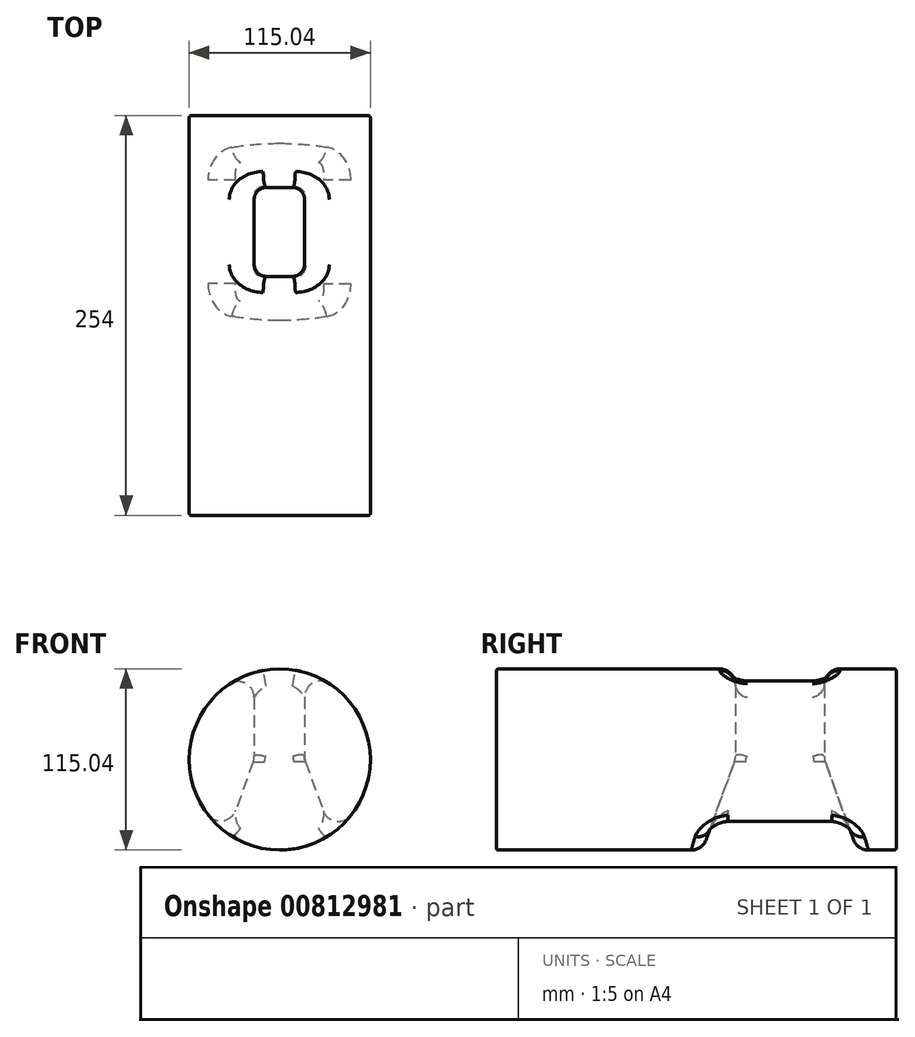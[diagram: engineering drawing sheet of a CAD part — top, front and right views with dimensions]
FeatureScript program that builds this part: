
annotation { "Feature Type Name" : "Feature", "Feature Type Description" : "" }
export const myFeature = defineFeature(function(context is Context, id is Id, definition is map)
    precondition{}
    {
        {
            var Q0;
            Q0=qCreatedBy(makeId("Front.planeOp"),FACE);
            var sketch = newSketch(context, id + "F0", { "sketchPlane" : qUnion([Q0])});
            skCircle(sketch, "E0", {"center": v(0, 0) * mm, "radius": 57.52 * mm});
            skSolve(sketch);
        }
        {
            var Q0;
            Q0 = qSketchRegion(id + "F0", true);
            extrude(context, id + "F1", {"entities" : qUnion([Q0]), "depth" : 254 * mm, "offsetDistance" : 25.4 * mm});
        }
        {
            var Q0;
            Q0=qCreatedBy(makeId("Top.planeOp"),FACE);
            var sketch = newSketch(context, id + "F2", { "sketchPlane" : qUnion([Q0])});
            skLineSegment(sketch, "E1.top", {"start": v(0, -45.7) * mm, "end": v(15.74, -45.7) * mm});
            skLineSegment(sketch, "E2.bottom", {"start": v(15.74, -45.7) * mm, "end": v(-16.26, -45.7) * mm});
            skLineSegment(sketch, "E2.top", {"start": v(15.74, -102.18) * mm, "end": v(-16.26, -102.18) * mm});
            skLineSegment(sketch, "E2.left", {"start": v(15.74, -45.7) * mm, "end": v(15.74, -102.18) * mm});
            skLineSegment(sketch, "E2.right", {"start": v(-16.26, -45.7) * mm, "end": v(-16.26, -102.18) * mm});
            skSolve(sketch);
        }
        {
            var Q0;
            Q0 = qSketchRegion(id + "F2", true);
            extrude(context, id + "F3", {"entities" : qUnion([Q0]), "operationType" : NewBodyOperationType.REMOVE, "oppositeDirection" : true, "depth" : 117.35 * mm, "offsetDistance" : 25.4 * mm, "hasDraft" : true, "draftAngle" : 20 * degree});
        }
        {
            var Q0;
            Q0=makeQuery(id+"F3.boolean.opBoolean","COPY",FACE,{"derivedFrom":makeQuery(id+"F3.opExtrude","CAP_FACE",FACE,{"disambiguationData":[OSD([sQuery(id+"F2.wireOp",EDGE,"E2.bottom"),sQuery(id+"F2.wireOp",EDGE,"E2.top"),sQuery(id+"F2.wireOp",EDGE,"E2.left"),sQuery(id+"F2.wireOp",EDGE,"E2.right")])],"isStart":true})});
            extrude(context, id + "F4", {"entities" : qUnion([Q0]), "operationType" : NewBodyOperationType.REMOVE, "oppositeDirection" : true, "depth" : 107.44 * mm, "offsetDistance" : 25.4 * mm});
        }
        {
            var Q0;
            Q0=makeQuery(id+"F3.boolean.opBoolean","COPY",EDGE,{"derivedFrom":makeQuery(id+"F3.opExtrude","SWEPT_EDGE",EDGE,{"disambiguationData":[OSD([sQuery(id+"F2.wireOp",EDGE,"E2.bottom"),sQuery(id+"F2.wireOp",EDGE,"E2.left")])]})});
            var Q1;
            Q1=makeQuery(id+"F3.boolean.opBoolean","COPY",EDGE,{"derivedFrom":makeQuery(id+"F3.opExtrude","SWEPT_EDGE",EDGE,{"disambiguationData":[OSD([sQuery(id+"F2.wireOp",EDGE,"E2.top"),sQuery(id+"F2.wireOp",EDGE,"E2.left")])]})});
            var Q2;
            Q2=makeQuery(id+"F3.boolean.opBoolean","COPY",EDGE,{"derivedFrom":makeQuery(id+"F3.opExtrude","SWEPT_EDGE",EDGE,{"disambiguationData":[OSD([sQuery(id+"F2.wireOp",EDGE,"E2.top"),sQuery(id+"F2.wireOp",EDGE,"E2.right")])]})});
            var Q3;
            Q3=makeQuery(id+"F3.boolean.opBoolean","COPY",EDGE,{"derivedFrom":makeQuery(id+"F3.opExtrude","SWEPT_EDGE",EDGE,{"disambiguationData":[OSD([sQuery(id+"F2.wireOp",EDGE,"E2.bottom"),sQuery(id+"F2.wireOp",EDGE,"E2.right")])]})});
            var Q4;
            Q4=makeQuery(id+"F4.boolean.opBoolean","COPY",EDGE,{"derivedFrom":makeQuery(id+"F4.opExtrude","SWEPT_EDGE",EDGE,{"disambiguationData":[OSD([sQuery(id+"F2.wireOp",EDGE,"E2.bottom"),sQuery(id+"F2.wireOp",EDGE,"E2.left")])]})});
            var Q5;
            Q5=makeQuery(id+"F4.boolean.opBoolean","COPY",EDGE,{"derivedFrom":makeQuery(id+"F4.opExtrude","SWEPT_EDGE",EDGE,{"disambiguationData":[OSD([sQuery(id+"F2.wireOp",EDGE,"E2.bottom"),sQuery(id+"F2.wireOp",EDGE,"E2.right")])]})});
            var Q6;
            Q6=makeQuery(id+"F4.boolean.opBoolean","COPY",EDGE,{"derivedFrom":makeQuery(id+"F4.opExtrude","SWEPT_EDGE",EDGE,{"disambiguationData":[OSD([sQuery(id+"F2.wireOp",EDGE,"E2.top"),sQuery(id+"F2.wireOp",EDGE,"E2.left")])]})});
            var Q7;
            Q7=makeQuery(id+"F4.boolean.opBoolean","COPY",EDGE,{"derivedFrom":makeQuery(id+"F4.opExtrude","SWEPT_EDGE",EDGE,{"disambiguationData":[OSD([sQuery(id+"F2.wireOp",EDGE,"E2.top"),sQuery(id+"F2.wireOp",EDGE,"E2.right")])]})});
            fillet(context, id + "F5", {"entities" : qUnion([Q0, Q1, Q2, Q3, Q4, Q5, Q6, Q7]), "radius" : 7.62 * mm, "tangentPropagation" : true, "allowEdgeOverflow" : false});
        }
        {
            var Q0;
            Q0=makeQuery(id+"F1.opExtrude","CAP_FACE",FACE,{"disambiguationData":[OSD([sQuery(id+"F0.wireOp",EDGE,"E0")])],"isStart":true});
            var Q1;
            Q1=makeQuery(id+"F1.opExtrude","CAP_EDGE",EDGE,{"disambiguationData":[OSD([sQuery(id+"F0.wireOp",EDGE,"E0")])],"isStart":false});
            fillet(context, id + "F6", {"entities" : qUnion([Q0, Q1]), "radius" : 1.27 * mm, "tangentPropagation" : true, "allowEdgeOverflow" : false});
        }
        {
            var Q0;
            Q0=makeQuery(id+"F3.boolean.opBoolean","INTERSECT",EDGE,{"derivedFrom":[makeQuery(id+"F1.opExtrude","SWEPT_FACE",FACE,{"disambiguationData":[OSD([sQuery(id+"F0.wireOp",EDGE,"E0")])]}),makeQuery(id+"F3.opExtrude","SWEPT_FACE",FACE,{"disambiguationData":[OSD([sQuery(id+"F2.wireOp",EDGE,"E2.left")])]})]});
            var Q1;
            {var subQ0=sQuery(id+"F2.wireOp",EDGE,"E2.left");Q1=makeQuery(id+"F4.boolean.opBoolean","MERGE",EDGE,{"derivedFrom":[makeQuery(id+"F3.boolean.opBoolean","COPY",EDGE,{"derivedFrom":makeQuery(id+"F3.opExtrude","CAP_EDGE",EDGE,{"disambiguationData":[OSD([subQ0])],"isStart":true})}),makeQuery(id+"F4.opExtrude","CAP_EDGE",EDGE,{"disambiguationData":[OSD([subQ0])],"isStart":true})]});}
            var Q2;
            Q2=makeQuery(id+"F4.boolean.opBoolean","INTERSECT",EDGE,{"derivedFrom":[makeQuery(id+"F1.opExtrude","SWEPT_FACE",FACE,{"disambiguationData":[OSD([sQuery(id+"F0.wireOp",EDGE,"E0")])]}),makeQuery(id+"F4.opExtrude","SWEPT_FACE",FACE,{"disambiguationData":[OSD([sQuery(id+"F2.wireOp",EDGE,"E2.left")])]})]});
            fillet(context, id + "F7", {"entities" : qUnion([Q0, Q1, Q2]), "radius" : 10.16 * mm, "tangentPropagation" : true, "allowEdgeOverflow" : false});
        }
    });
